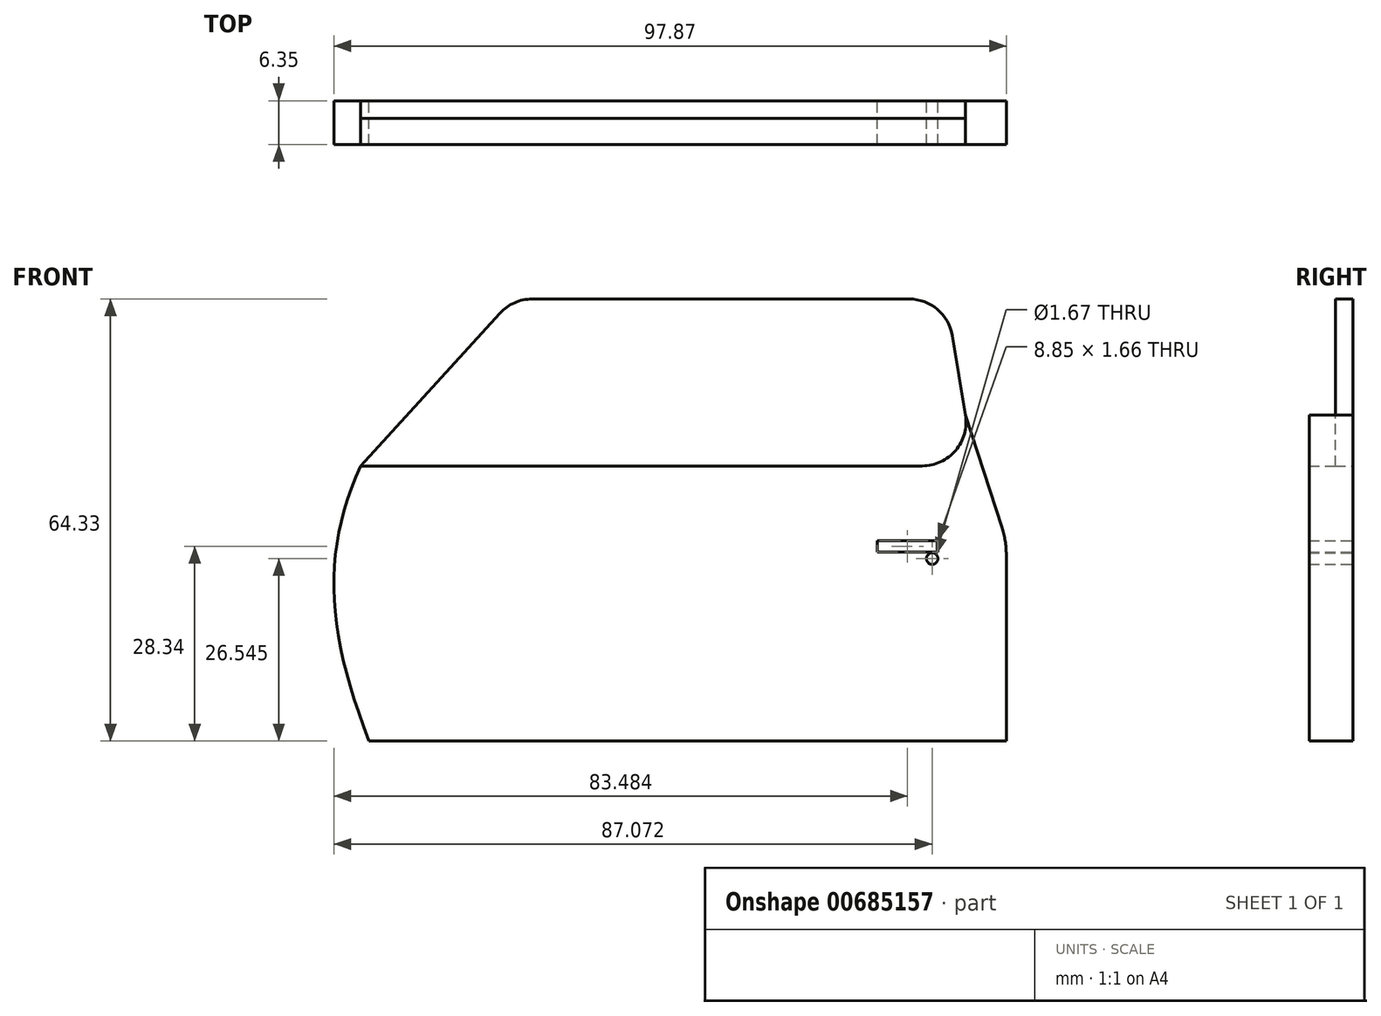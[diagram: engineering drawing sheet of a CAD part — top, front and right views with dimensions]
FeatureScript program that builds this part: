
annotation { "Feature Type Name" : "Feature", "Feature Type Description" : "" }
export const myFeature = defineFeature(function(context is Context, id is Id, definition is map)
    precondition{}
    {
        {
            var Q0;
            Q0=qCreatedBy(makeId("Front.planeOp"),FACE);
            var sketch = newSketch(context, id + "F0", { "sketchPlane" : qUnion([Q0])});
            skLineSegment(sketch, "E0.bottom", {"start": v(-20.93, -25.39) * mm, "end": v(71.82, -25.39) * mm});
            skLineSegment(sketch, "E0.top", {"start": v(-22.14, 14.65) * mm, "end": v(59.6, 14.65) * mm});
            skLineSegment(sketch, "E0.right", {"start": v(71.82, -25.39) * mm, "end": v(71.8, 1.76) * mm});
            skPoint(sketch, "E1.middle", {"position": v(-152.88, 61.71) * mm});
            skFitSpline(sketch, "E2", {"points": [v(-20.93, -25.39) * mm, v(-22.14, 14.65) * mm], "startDerivative": vector(-18.74, 48.67) * mm, "endDerivative": vector(17.18, 37.91) * mm});
            skLineSegment(sketch, "E3.bottom", {"start": v(53, 3.78) * mm, "end": v(61.86, 3.78) * mm});
            skLineSegment(sketch, "E3.top", {"start": v(53, 2.12) * mm, "end": v(61.86, 2.12) * mm});
            skLineSegment(sketch, "E3.left", {"start": v(53, 3.78) * mm, "end": v(53, 2.12) * mm});
            skLineSegment(sketch, "E3.right", {"start": v(61.86, 3.78) * mm, "end": v(61.86, 2.12) * mm});
            skCircle(sketch, "E4", {"center": v(61.02, 1.16) * mm, "radius": 0.84 * mm});
            skLineSegment(sketch, "E5.bottom", {"start": v(60.85, 1.62) * mm, "end": v(61.2, 1.62) * mm});
            skLineSegment(sketch, "E5.top", {"start": v(60.85, 0.76) * mm, "end": v(61.2, 0.76) * mm});
            skLineSegment(sketch, "E5.left", {"start": v(60.85, 1.62) * mm, "end": v(60.85, 0.76) * mm});
            skLineSegment(sketch, "E5.right", {"start": v(61.2, 1.62) * mm, "end": v(61.2, 0.76) * mm});
            skLineSegment(sketch, "E6", {"start": v(-22.14, 14.65) * mm, "end": v(-1.89, 36.87) * mm});
            skPoint(sketch, "E7.visualSharp", {"position": v(0, 38.94) * mm});
            skArc(sketch, "E7.filletArc", {"start": v(2.8, 38.94) * mm, "mid": v(0.24, 38.4) * mm, "end": v(-1.89, 36.87) * mm});
            skLineSegment(sketch, "E8", {"start": v(2.8, 38.94) * mm, "end": v(57.67, 38.94) * mm});
            skLineSegment(sketch, "E9", {"start": v(63.94, 33.63) * mm, "end": v(65.86, 22.04) * mm});
            skPoint(sketch, "E10.visualSharp", {"position": v(63.06, 38.94) * mm});
            skArc(sketch, "E10.filletArc", {"start": v(63.94, 33.63) * mm, "mid": v(61.78, 37.43) * mm, "end": v(57.67, 38.94) * mm});
            skArc(sketch, "E11.filletArc", {"start": v(59.6, 14.65) * mm, "mid": v(64.44, 16.9) * mm, "end": v(65.86, 22.04) * mm});
            skLineSegment(sketch, "E12", {"start": v(65.86, 22.04) * mm, "end": v(71.18, 5.68) * mm});
            skArc(sketch, "E13.filletArc", {"start": v(71.8, 1.76) * mm, "mid": v(71.64, 3.74) * mm, "end": v(71.18, 5.68) * mm});
            skSolve(sketch);
        }
        {
            var Q0;
            Q0=makeQuery(id+"F0.imprint","IMPRINT",FACE,{"disambiguationData":[TD([[makeQuery(id+"F0.imprint","IMPRINT",EDGE,{"derivedFrom":sQuery(id+"F0.wireOp",EDGE,"E0.bottom")}),1.0]])]});
            extrude(context, id + "F1", {"entities" : qUnion([Q0]), "depth" : 6.35 * mm, "offsetDistance" : 25.4 * mm});
        }
        {
            var Q0;
            Q0 = qSketchRegion(id + "F0", true);
            extrude(context, id + "F2", {"entities" : qUnion([Q0]), "operationType" : NewBodyOperationType.ADD, "depth" : 2.54 * mm, "offsetDistance" : 25.4 * mm});
        }
    });
